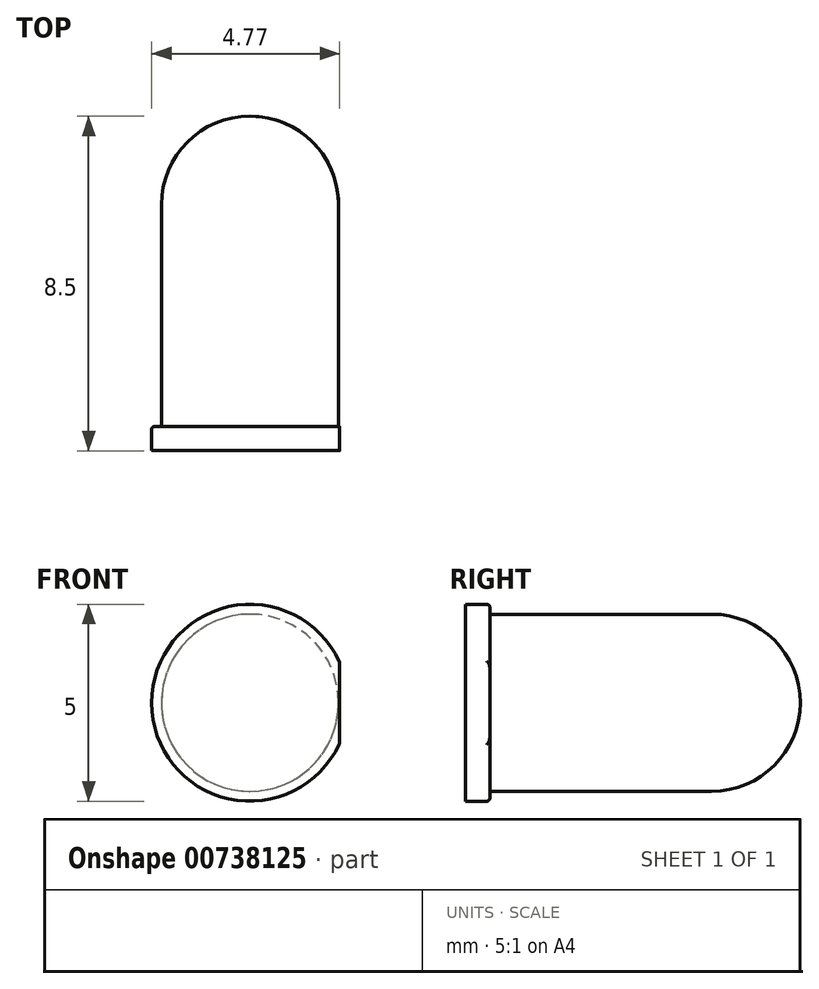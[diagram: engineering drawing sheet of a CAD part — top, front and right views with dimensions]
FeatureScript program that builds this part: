
annotation { "Feature Type Name" : "Feature", "Feature Type Description" : "" }
export const myFeature = defineFeature(function(context is Context, id is Id, definition is map)
    precondition{}
    {
        {
            var Q0;
            Q0=qCreatedBy(makeId("Top.planeOp"),FACE);
            var sketch = newSketch(context, id + "F0", { "sketchPlane" : qUnion([Q0])});
            skLineSegment(sketch, "E0", {"start": v(-101.5, -9.97) * mm, "end": v(-101.5, -18.47) * mm});
            skArc(sketch, "E1", {"start": v(-101.5, -9.97) * mm, "mid": v(-103.75, -12.22) * mm, "end": v(-101.5, -14.47) * mm});
            skLineSegment(sketch, "E2.bottom", {"start": v(-101.5, -18.47) * mm, "end": v(-104, -18.47) * mm});
            skLineSegment(sketch, "E2.top", {"start": v(-101.5, -17.85) * mm, "end": v(-104, -17.85) * mm});
            skLineSegment(sketch, "E2.left", {"start": v(-101.5, -18.47) * mm, "end": v(-101.5, -17.85) * mm});
            skLineSegment(sketch, "E2.right", {"start": v(-104, -18.47) * mm, "end": v(-104, -17.85) * mm});
            skLineSegment(sketch, "E3", {"start": v(-103.75, -12.22) * mm, "end": v(-103.75, -17.85) * mm});
            skSolve(sketch);
        }
        {
            var Q0;
            {var subQ0=sQuery(id+"F0.wireOp",EDGE,"E1");var subQ1=sQuery(id+"F0.wireOp",EDGE,"E0");var subQ5=sQuery(id+"F0.wireOp",EDGE,"E3");var subQ10=sQuery(id+"F0.wireOp",EDGE,"E2.bottom");var subQ12=makeQuery(id+"F0.imprint","INTERSECT",VERTEX,{"disambiguationData":[OD(0.0)],"derivedFrom":[subQ1,subQ0]});Q0=qUnion([makeQuery(id+"F0.imprint","IMPRINT",FACE,{"disambiguationData":[TD([[makeQuery(id+"F0.imprint","IMPRINT",EDGE,{"disambiguationData":[TD([[subQ12,-1.0]])],"derivedFrom":subQ1}),-1.0]])]}),makeQuery(id+"F0.imprint","IMPRINT",FACE,{"disambiguationData":[TD([[makeQuery(id+"F0.imprint","IMPRINT",EDGE,{"derivedFrom":subQ10}),-1.0]])]}),makeQuery(id+"F0.imprint","IMPRINT",FACE,{"disambiguationData":[TD([[makeQuery(id+"F0.imprint","IMPRINT",EDGE,{"derivedFrom":subQ5}),1.0]])]})]);}
            var Q1;
            Q1=sQuery(id+"F0.wireOp",EDGE,"E0");
            revolve(context, id + "F1", {"entities" : qUnion([Q0]), "axis" : qUnion([Q1]), "revolveType" : RevolveType.FULL});
        }
        {
            var Q0;
            Q0=qCreatedBy(makeId("Top.planeOp"),FACE);
            var sketch = newSketch(context, id + "F2", { "sketchPlane" : qUnion([Q0])});
            skLineSegment(sketch, "E4.0", {"start": v(-104, -17.85) * mm, "end": v(-99, -17.85) * mm});
            skLineSegment(sketch, "E4.1", {"start": v(-104, -18.47) * mm, "end": v(-99, -18.47) * mm});
            skLineSegment(sketch, "E5", {"start": v(-99, -17.85) * mm, "end": v(-99, -18.47) * mm});
            skLineSegment(sketch, "E6", {"start": v(-99.23, -17.85) * mm, "end": v(-99.23, -18.47) * mm});
            skSolve(sketch);
        }
        {
            var Q0;
            Q0=qSketchRegion(id+"F2",true);
            extrude(context, id + "F3", {"entities" : qUnion([Q0]), "operationType" : NewBodyOperationType.REMOVE, "oppositeDirection" : true, "depth" : 25 * mm, "symmetric" : true});
        }
        {
            var Q0;
            Q0=makeQuery(id+"F1.opRevolve","SWEPT_EDGE",EDGE,{"disambiguationData":[OSD([sQuery(id+"F0.wireOp",EDGE,"E2.top"),sQuery(id+"F0.wireOp",EDGE,"E2.right")])]});
            var Q1;
            Q1=makeQuery(id+"F3.boolean.opBoolean","COPY",EDGE,{"derivedFrom":makeQuery(id+"F3.opExtrude","SWEPT_EDGE",EDGE,{"disambiguationData":[OSD([sQuery(id+"F2.wireOp",EDGE,"E4.0"),sQuery(id+"F2.wireOp",EDGE,"E6")])]})});
            var Q2;
            Q2=makeQuery(id+"F3.boolean.opBoolean","INTERSECT",EDGE,{"disambiguationData":[OD(1.0)],"derivedFrom":[makeQuery(id+"F1.opRevolve","SWEPT_FACE",FACE,{"disambiguationData":[OSD([sQuery(id+"F0.wireOp",EDGE,"E2.right")])]}),makeQuery(id+"F3.opExtrude","SWEPT_FACE",FACE,{"disambiguationData":[OSD([sQuery(id+"F2.wireOp",EDGE,"E6")])]})]});
            var Q3;
            Q3=makeQuery(id+"F3.boolean.opBoolean","INTERSECT",EDGE,{"disambiguationData":[OD(0.0)],"derivedFrom":[makeQuery(id+"F1.opRevolve","SWEPT_FACE",FACE,{"disambiguationData":[OSD([sQuery(id+"F0.wireOp",EDGE,"E2.right")])]}),makeQuery(id+"F3.opExtrude","SWEPT_FACE",FACE,{"disambiguationData":[OSD([sQuery(id+"F2.wireOp",EDGE,"E6")])]})]});
            fillet(context, id + "F4", {"entities" : qUnion([Q0, Q1, Q2, Q3]), "radius" : 0.07 * mm, "tangentPropagation" : true, "allowEdgeOverflow" : false});
        }
    });
